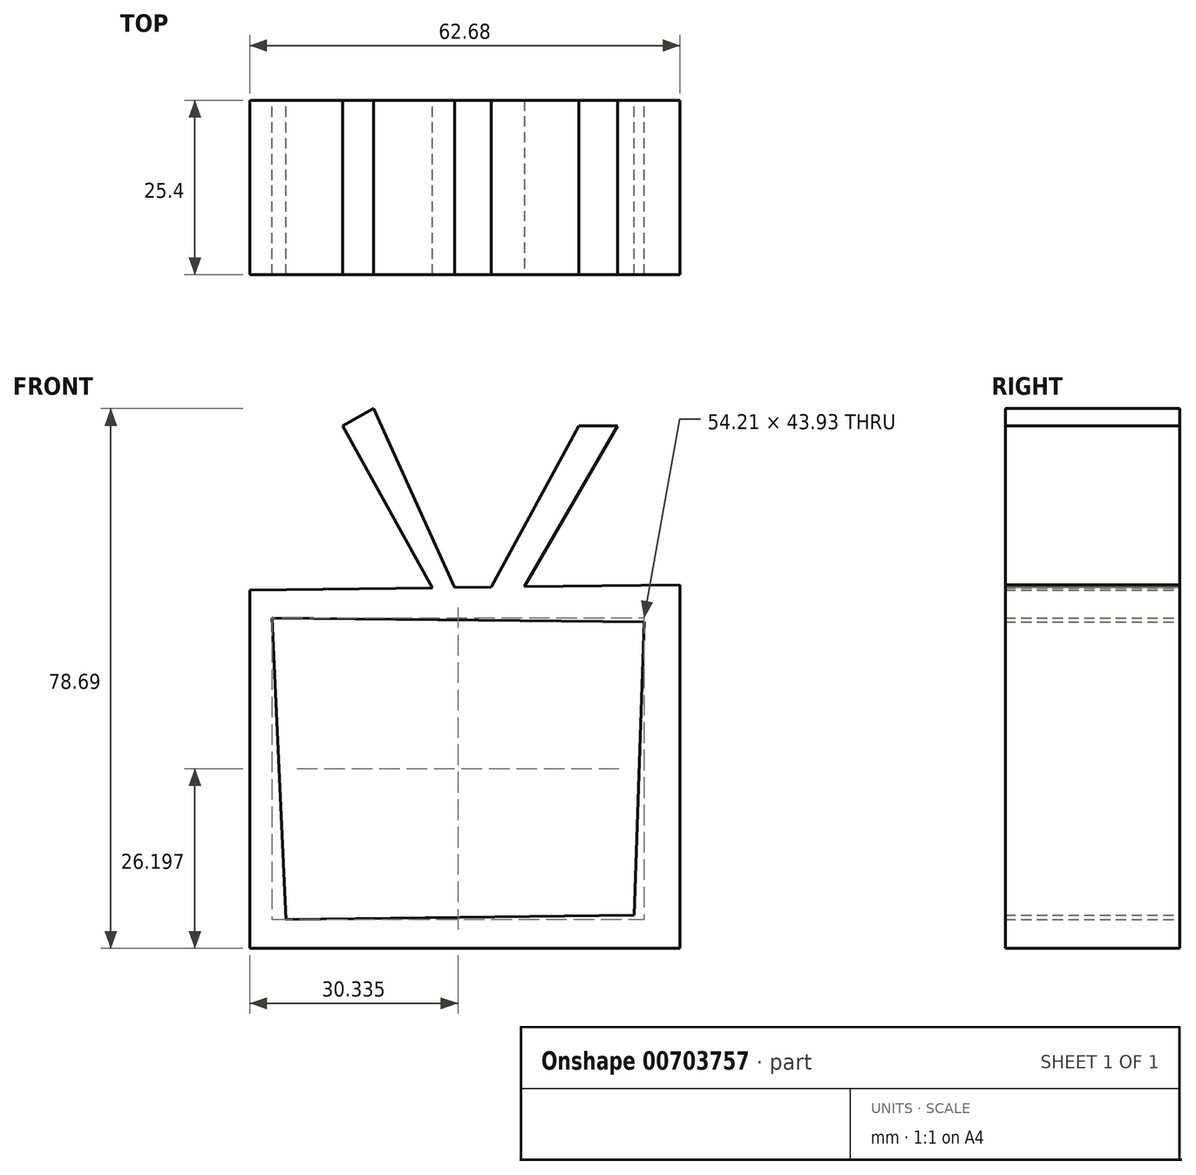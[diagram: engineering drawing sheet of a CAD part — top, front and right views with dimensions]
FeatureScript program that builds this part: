
annotation { "Feature Type Name" : "Feature", "Feature Type Description" : "" }
export const myFeature = defineFeature(function(context is Context, id is Id, definition is map)
    precondition{}
    {
        {
            var Q0;
            Q0=qCreatedBy(makeId("Front.planeOp"),FACE);
            var sketch = newSketch(context, id + "F0", { "sketchPlane" : qUnion([Q0])});
            skLineSegment(sketch, "E0", {"start": v(-34.97, 13.8) * mm, "end": v(-34.97, -38.4) * mm});
            skLineSegment(sketch, "E1", {"start": v(-34.97, -38.4) * mm, "end": v(27.71, -38.4) * mm});
            skLineSegment(sketch, "E2", {"start": v(27.71, -38.4) * mm, "end": v(27.71, 14.61) * mm});
            skLineSegment(sketch, "E3", {"start": v(28.72, 14.61) * mm, "end": v(-34.97, 13.8) * mm});
            skLineSegment(sketch, "E4", {"start": v(-31.74, 9.77) * mm, "end": v(-29.73, -34.16) * mm});
            skLineSegment(sketch, "E5", {"start": v(-29.73, -34.16) * mm, "end": v(21.05, -33.52) * mm});
            skLineSegment(sketch, "E6", {"start": v(21.05, -33.52) * mm, "end": v(22.47, 9.17) * mm});
            skLineSegment(sketch, "E7", {"start": v(22.47, 9.17) * mm, "end": v(-31.74, 9.77) * mm});
            skSolve(sketch);
        }
        {
            var Q0;
            Q0 = qSketchRegion(id + "F0", true);
            extrude(context, id + "F1", {"entities" : qUnion([Q0]), "depth" : 25.4 * mm, "offsetDistance" : 25.4 * mm});
        }
        {
            var Q0;
            Q0=qCreatedBy(makeId("Front.planeOp"),FACE);
            var sketch = newSketch(context, id + "F2", { "sketchPlane" : qUnion([Q0])});
            skLineSegment(sketch, "E8", {"start": v(-8.16, 13.8) * mm, "end": v(-21.46, 37.79) * mm});
            skLineSegment(sketch, "E9", {"start": v(-21.46, 37.79) * mm, "end": v(-16.93, 40.3) * mm});
            skLineSegment(sketch, "E10", {"start": v(-16.93, 40.3) * mm, "end": v(-4.94, 13.8) * mm});
            skLineSegment(sketch, "E11", {"start": v(-4.94, 13.8) * mm, "end": v(-8.16, 13.8) * mm});
            skLineSegment(sketch, "E12", {"start": v(0, 13.8) * mm, "end": v(13, 37.79) * mm});
            skLineSegment(sketch, "E13", {"start": v(13, 37.79) * mm, "end": v(18.64, 37.79) * mm});
            skLineSegment(sketch, "E14", {"start": v(18.64, 37.79) * mm, "end": v(4.74, 13.8) * mm});
            skLineSegment(sketch, "E15", {"start": v(4.74, 13.8) * mm, "end": v(0, 13.8) * mm});
            skSolve(sketch);
        }
        {
            var Q0;
            Q0 = qSketchRegion(id + "F2", true);
            extrude(context, id + "F3", {"entities" : qUnion([Q0]), "operationType" : NewBodyOperationType.ADD, "depth" : 25.4 * mm, "offsetDistance" : 25.4 * mm});
        }
    });
